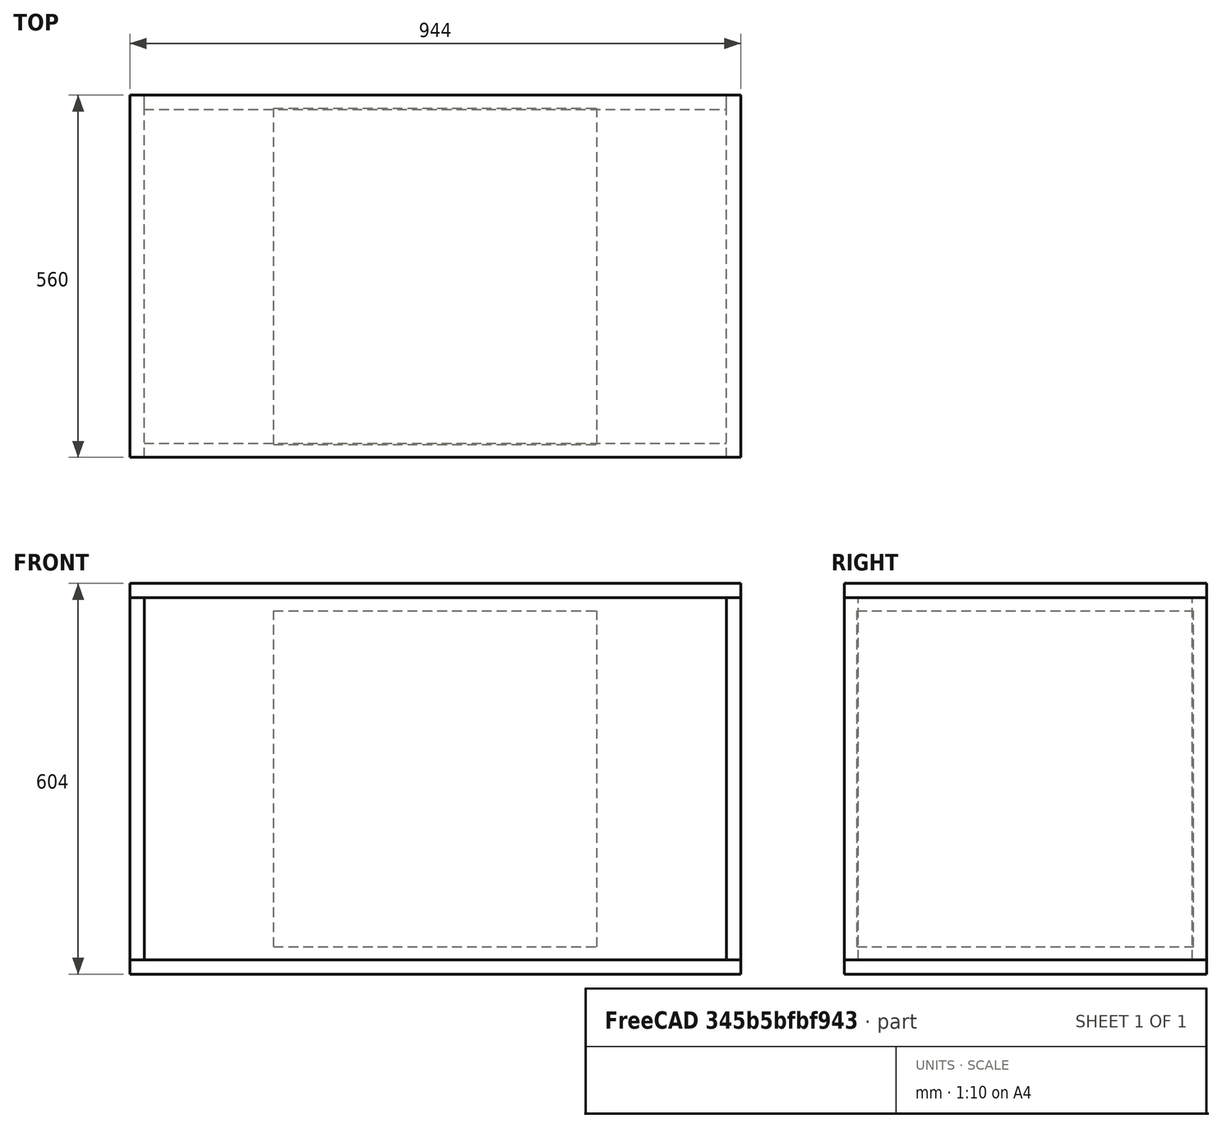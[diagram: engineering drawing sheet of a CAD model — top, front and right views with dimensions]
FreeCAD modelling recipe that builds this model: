
FCSTD DOCUMENT  (FreeCAD 0.21R0.21.2)
Label: MDFHousing
License: All rights reserved
LicenseURL: http://en.wikipedia.org/wiki/All_rights_reserved
objects: Part::Box×7
note: 7 computed .brp shape members not serialized (recipe doc carries the construction recipe); baked Part::Feature solids carry a one-line shape summary decoded from their .brp

FEATURE [Part::Box] Box  label="Cube"
  AttacherType = Attacher::AttachEngine3D
  Height = 520
  Length = 500
  Placement = pos=(-250,-260,42) rot=(0,0,1;0rad)
  Width = 520
FEATURE [Part::Box] Box001  label="Cube001"
  AttacherType = Attacher::AttachEngine3D
  Height = 22
  Length = 944
  Placement = pos=(-472,-280,0) rot=(0,0,1;0rad)
  Width = 560
FEATURE [Part::Box] Box002  label="Cube002"
  AttacherType = Attacher::AttachEngine3D
  Height = 22
  Length = 944
  Placement = pos=(-472,-280,582) rot=(0,0,1;0rad)
  Width = 560
FEATURE [Part::Box] Box003  label="Cube003"
  AttacherType = Attacher::AttachEngine3D
  Height = 560
  Length = 22
  Placement = pos=(-472,-280,22) rot=(0,0,1;0rad)
  Width = 560
FEATURE [Part::Box] Box004  label="Cube004"
  AttacherType = Attacher::AttachEngine3D
  Height = 560
  Length = 22
  Placement = pos=(450,-280,22) rot=(0,0,1;0rad)
  Width = 560
FEATURE [Part::Box] Box005  label="Cube005"
  AttacherType = Attacher::AttachEngine3D
  Height = 560
  Length = 900
  Placement = pos=(-450,258,22) rot=(0,0,1;0rad)
  Width = 22
FEATURE [Part::Box] Box006  label="Cube006"
  AttacherType = Attacher::AttachEngine3D
  Height = 560
  Length = 900
  Placement = pos=(-450,-280,22) rot=(0,0,1;0rad)
  Width = 22
